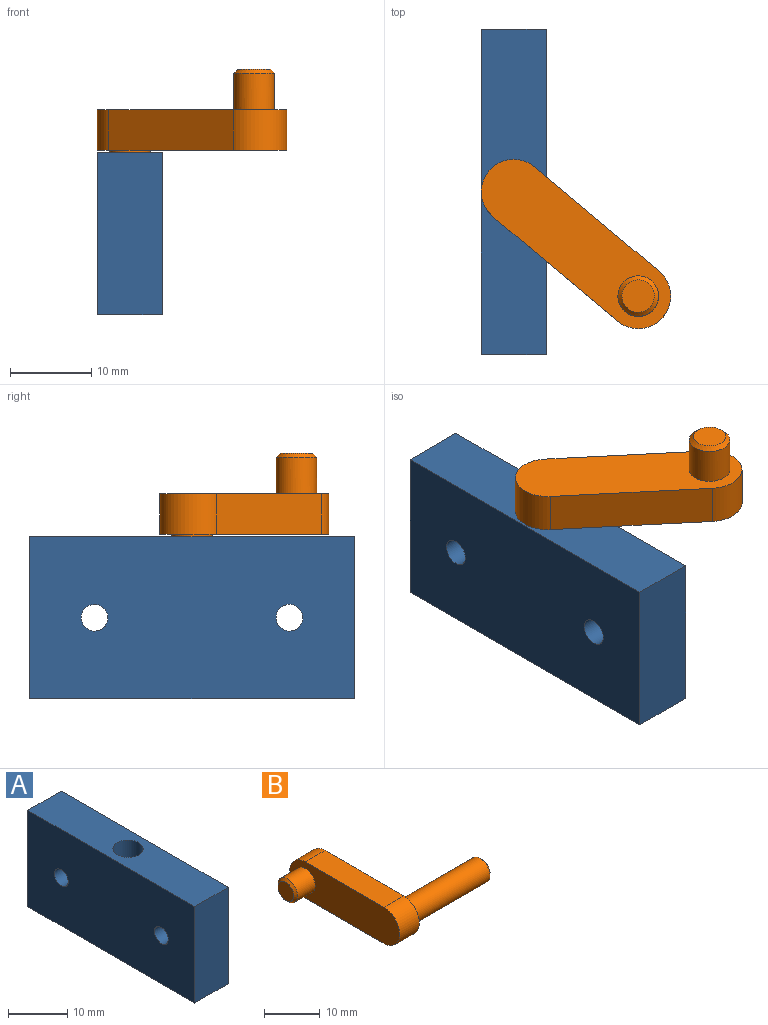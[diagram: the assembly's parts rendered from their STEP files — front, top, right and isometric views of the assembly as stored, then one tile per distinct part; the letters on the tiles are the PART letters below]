
ASSEMBLY  parts=2 mates=1
PART A: 11 faces, bbox 8x40x20 mm
  f0: plane 20x8mm, normal (0,-1,0), area 160mm2, adj f1,f5,f6,f7
  f1: plane 40x8mm, normal (0,0,-1), area 299.6mm2, adj f0,f2,f6,f7,f10
  f2: plane 20x8mm, normal (0,1,0), area 160mm2, adj f1,f5,f6,f7
  f3: cylinder r=1.65mm len=5mm, axis (-1,0,0), area 51.8mm2, adj f7,f9
  f4: cylinder r=1.65mm len=5mm, axis (-1,0,0), area 51.8mm2, adj f7,f8
  f5: plane 40x8mm, normal (0,0,1), area 299.6mm2, adj f0,f2,f6,f7,f10
  f6: plane 40x20mm, normal (1,0,0), area 664.1mm2, adj f0,f1,f2,f5,f8,f9
  f7: plane 40x20mm, normal (-1,0,0), area 782.9mm2, adj f0,f1,f2,f3,f4,f5
  f8: cone r=1.65mm half-angle=45deg, axis (1,0,0), area 84mm2, adj f4,f6
  f9: cone r=1.65mm half-angle=45deg, axis (1,0,0), area 84mm2, adj f3,f6
  f10: cylinder r=2.55mm len=20mm, axis (0,0,-1), area 320.4mm2, adj f1,f5
PART B: 12 faces, bbox 30x28x8 mm
  f0: cylinder r=2.5mm len=19.5mm, axis (-1,0,0), area 306.3mm2, adj f6,f10
  f1: plane 4x4mm, normal (1,0,0), area 12.6mm2, adj f10
  f2: plane 20x5mm, normal (0,0,1), area 100mm2, adj f3,f5,f6,f7
  f3: cylinder r=4mm len=8mm, axis (-1,0,0), area 62.8mm2, adj f2,f4,f6,f7
  f4: plane 20x5mm, normal (0,0,-1), area 100mm2, adj f3,f5,f6,f7
  f5: cylinder r=4mm len=8mm, axis (-1,0,0), area 62.8mm2, adj f2,f4,f6,f7
  f6: plane 28x8mm, normal (1,0,0), area 190.6mm2, adj f0,f2,f3,f4,f5
  f7: plane 28x8mm, normal (-1,0,0), area 190.6mm2, adj f2,f3,f4,f5,f8
  f8: cylinder r=2.5mm len=5mm, axis (1,0,0), area 70.7mm2, adj f7,f11
  f9: plane 4x4mm, normal (-1,0,0), area 12.6mm2, adj f11
  f10: cone r=2mm half-angle=45deg, axis (-1,0,0), area 10mm2, adj f0,f1
  f11: cone r=2.5mm half-angle=45deg, axis (1,0,0), area 10mm2, adj f8,f9
PLACE A t=(-31.91,36.36,23.34)mm
PLACE B rot(axis=(0.67,0.31,-0.67),145.2deg) t=(-30.97,38.93,38.61)mm
MATE cylindrical A.f10 <-> B.f0  axis (0,0,1) through (-27.91,36.36,33.34)mm
